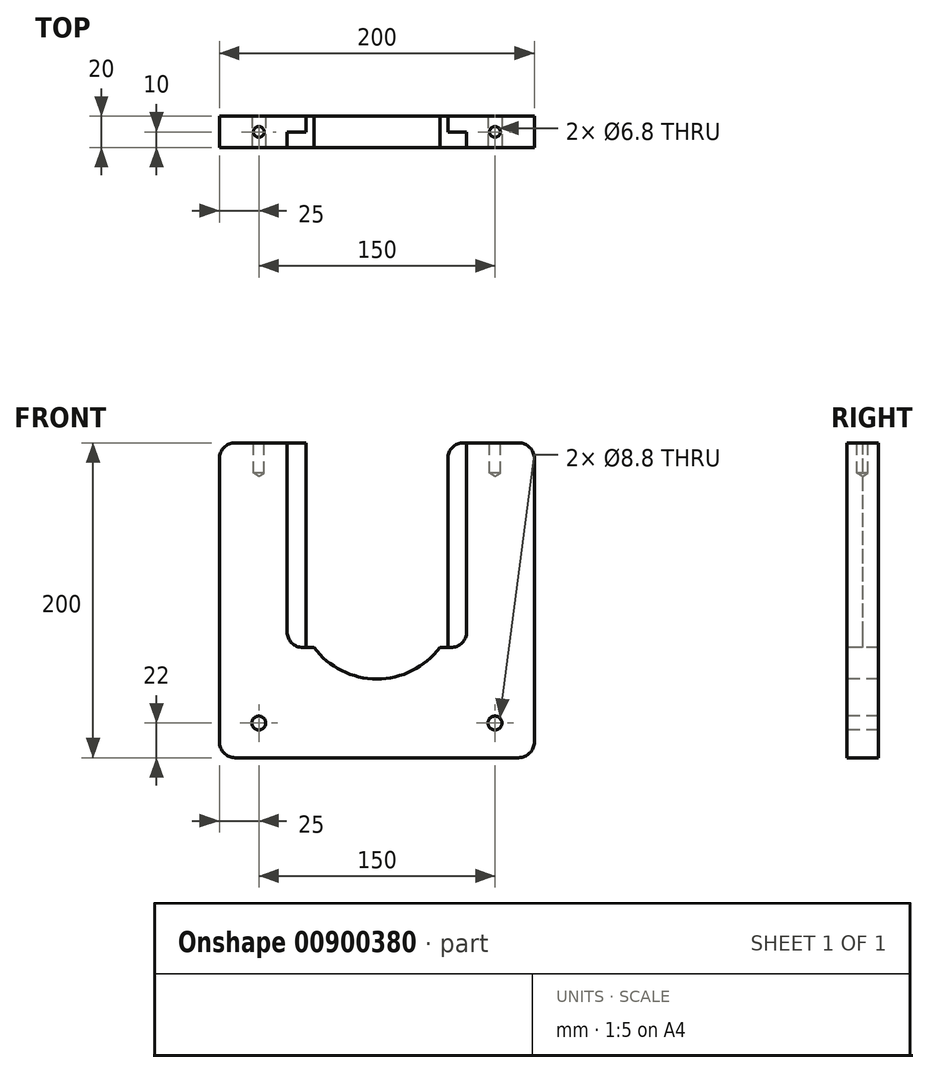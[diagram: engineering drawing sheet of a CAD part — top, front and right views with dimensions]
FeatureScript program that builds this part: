
annotation { "Feature Type Name" : "Feature", "Feature Type Description" : "" }
export const myFeature = defineFeature(function(context is Context, id is Id, definition is map)
    precondition{}
    {
        {
            var Q0;
            Q0=qCreatedBy(makeId("Front.planeOp"),FACE);
            var sketch = newSketch(context, id + "F0", { "sketchPlane" : qUnion([Q0])});
            skLineSegment(sketch, "E0.bottom", {"start": v(-100, 100) * mm, "end": v(100, 100) * mm});
            skLineSegment(sketch, "E0.top", {"start": v(-100, -100) * mm, "end": v(100, -100) * mm});
            skLineSegment(sketch, "E0.left", {"start": v(-100, 100) * mm, "end": v(-100, -100) * mm});
            skLineSegment(sketch, "E0.right", {"start": v(100, 100) * mm, "end": v(100, -100) * mm});
            skPoint(sketch, "E0.middle", {"position": v(0, 0) * mm});
            skSolve(sketch);
        }
        {
            var Q0;
            Q0=qSketchRegion(id+"F0",true);
            extrude(context, id + "F1", {"entities" : qUnion([Q0]), "endBound" : BoundingType.SYMMETRIC, "depth" : 20 * mm, "offsetDistance" : 25 * mm});
        }
        {
            var Q0;
            Q0=makeQuery(id+"F1.opExtrude","CAP_FACE",FACE,{"disambiguationData":[OSD([sQuery(id+"F0.wireOp",EDGE,"E0.bottom"),sQuery(id+"F0.wireOp",EDGE,"E0.top"),sQuery(id+"F0.wireOp",EDGE,"E0.left"),sQuery(id+"F0.wireOp",EDGE,"E0.right")])],"isStart":false});
            var sketch = newSketch(context, id + "F2", { "sketchPlane" : qUnion([Q0])});
            skCircle(sketch, "E1", {"center": v(0, 0) * mm, "radius": 15 * mm});
            skCircle(sketch, "E2", {"center": v(0, 0) * mm, "radius": 75 * mm, "construction": true});
            skSolve(sketch);
        }
        {
            var Q0;
            Q0=qSketchRegion(id+"F2",true);
            extrude(context, id + "F3", {"entities" : qUnion([Q0]), "operationType" : NewBodyOperationType.REMOVE, "endBound" : BoundingType.THROUGH_ALL, "oppositeDirection" : true, "depth" : 25 * mm, "offsetDistance" : 25 * mm});
        }
        {
            var Q0;
            Q0=makeQuery(id+"F1.opExtrude","CAP_FACE",FACE,{"disambiguationData":[OSD([sQuery(id+"F0.wireOp",EDGE,"E0.bottom"),sQuery(id+"F0.wireOp",EDGE,"E0.top"),sQuery(id+"F0.wireOp",EDGE,"E0.left"),sQuery(id+"F0.wireOp",EDGE,"E0.right")])],"isStart":false});
            var sketch = newSketch(context, id + "F4", { "sketchPlane" : qUnion([Q0])});
            skPoint(sketch, "E3", {"position": v(75, -78) * mm});
            skPoint(sketch, "E4", {"position": v(-75, -78) * mm});
            skPoint(sketch, "E5", {"position": v(0, 0) * mm});
            skSolve(sketch);
        }
        {
            var Q0;
            Q0=sQuery(id+"F4.wireOp",VERTEX,"0a962e41-9311-4d20-8398-ac3b29eb1dd7");
            var Q1;
            Q1=sQuery(id+"F4.wireOp",VERTEX,"E4");
            var Q2;
            Q2=sQuery(id+"F4.wireOp",VERTEX,"E3");
            var Q3;
            Q3=makeQuery(id+"F1.opExtrude","SWEPT_BODY",BODY,{"disambiguationData":[OSD([sQuery(id+"F0.wireOp",EDGE,"E0.bottom"),sQuery(id+"F0.wireOp",EDGE,"E0.top"),sQuery(id+"F0.wireOp",EDGE,"E0.left"),sQuery(id+"F0.wireOp",EDGE,"E0.right")])]});
            hole(context, id + "F5", {"style" : HoleStyle.SIMPLE, "endStyle" : HoleEndStyle.THROUGH, "standardTappedOrClearance" : lookupTablePath({ "standard" : "ISO", "engagement" : "75%", "pitch" : "1.25 mm", "size" : "M10", "type" : "Tapped" }), "standardBlindInLast" : lookupTablePath({ "standard" : "ISO", "engagement" : "75%", "pitch" : "1.25 mm", "size" : "M10", "type" : "Tapped" }), "holeDiameter" : 8.8 * mm, "majorDiameter" : 10 * mm, "showTappedDepth" : true, "isTappedThrough" : true, "tappedDepth" : 12 * mm, "tapClearance" : 3, "startFromSketch" : true, "locations" : qUnion([Q0, Q1, Q2]), "scope" : qUnion([Q3])});
        }
        {
            var Q0;
            Q0=makeQuery(id+"F1.opExtrude","CAP_FACE",FACE,{"disambiguationData":[OSD([sQuery(id+"F0.wireOp",EDGE,"E0.bottom"),sQuery(id+"F0.wireOp",EDGE,"E0.top"),sQuery(id+"F0.wireOp",EDGE,"E0.left"),sQuery(id+"F0.wireOp",EDGE,"E0.right")])],"isStart":false});
            var sketch = newSketch(context, id + "F6", { "sketchPlane" : qUnion([Q0])});
            skLineSegment(sketch, "E6.bottom", {"start": v(-45, 100) * mm, "end": v(45, 100) * mm});
            skLineSegment(sketch, "E6.left", {"start": v(-45, 100) * mm, "end": v(-45, -30) * mm});
            skLineSegment(sketch, "E6.right", {"start": v(45, 100) * mm, "end": v(45, -30) * mm});
            skLineSegment(sketch, "E7", {"start": v(0, 0) * mm, "end": v(0, 100) * mm, "construction": true});
            skArc(sketch, "E8", {"start": v(-40, -30) * mm, "mid": v(0, -50) * mm, "end": v(40, -30) * mm});
            skLineSegment(sketch, "E9", {"start": v(40, -30) * mm, "end": v(45, -30) * mm});
            skLineSegment(sketch, "E10", {"start": v(-40, -30) * mm, "end": v(-45, -30) * mm});
            skSolve(sketch);
        }
        {
            var Q0;
            Q0=qSketchRegion(id+"F6",true);
            extrude(context, id + "F7", {"entities" : qUnion([Q0]), "operationType" : NewBodyOperationType.REMOVE, "endBound" : BoundingType.THROUGH_ALL, "oppositeDirection" : true, "depth" : 25 * mm, "offsetDistance" : 25 * mm});
        }
        {
            var Q0;
            Q0=makeQuery(id+"F1.opExtrude","CAP_FACE",FACE,{"disambiguationData":[OSD([sQuery(id+"F0.wireOp",EDGE,"E0.bottom"),sQuery(id+"F0.wireOp",EDGE,"E0.top"),sQuery(id+"F0.wireOp",EDGE,"E0.left"),sQuery(id+"F0.wireOp",EDGE,"E0.right")])],"isStart":false});
            var sketch = newSketch(context, id + "F8", { "sketchPlane" : qUnion([Q0])});
            skLineSegment(sketch, "E11.bottom", {"start": v(-57, 100) * mm, "end": v(-45, 100) * mm});
            skLineSegment(sketch, "E11.top", {"start": v(-57, -30) * mm, "end": v(-45, -30) * mm});
            skLineSegment(sketch, "E11.left", {"start": v(-57, 100) * mm, "end": v(-57, -30) * mm});
            skLineSegment(sketch, "E11.right", {"start": v(-45, 100) * mm, "end": v(-45, -30) * mm});
            skLineSegment(sketch, "E12.bottom", {"start": v(57, 100) * mm, "end": v(45, 100) * mm});
            skLineSegment(sketch, "E12.top", {"start": v(57, -30) * mm, "end": v(45, -30) * mm});
            skLineSegment(sketch, "E12.left", {"start": v(57, 100) * mm, "end": v(57, -30) * mm});
            skLineSegment(sketch, "E12.right", {"start": v(45, 100) * mm, "end": v(45, -30) * mm});
            skSolve(sketch);
        }
        {
            var Q0;
            Q0=qSketchRegion(id+"F8",true);
            extrude(context, id + "F9", {"entities" : qUnion([Q0]), "operationType" : NewBodyOperationType.REMOVE, "oppositeDirection" : true, "depth" : 10 * mm, "offsetDistance" : 25 * mm});
        }
        {
            var Q0;
            Q0=makeQuery(id+"F1.opExtrude","SWEPT_EDGE",EDGE,{"disambiguationData":[OSD([sQuery(id+"F0.wireOp",EDGE,"E0.bottom"),sQuery(id+"F0.wireOp",EDGE,"E0.left")])]});
            var Q1;
            Q1=makeQuery(id+"F7.boolean.opBoolean","COPY",EDGE,{"derivedFrom":makeQuery(id+"F7.opExtrude","SWEPT_EDGE",EDGE,{"disambiguationData":[OSD([sQuery(id+"F0.wireOp",EDGE,"E0.bottom"),sQuery(id+"F6.wireOp",EDGE,"E6.bottom"),sQuery(id+"F6.wireOp",EDGE,"E6.left")])]})});
            var Q2;
            Q2=makeQuery(id+"F7.boolean.opBoolean","COPY",EDGE,{"derivedFrom":makeQuery(id+"F7.opExtrude","SWEPT_EDGE",EDGE,{"disambiguationData":[OSD([sQuery(id+"F0.wireOp",EDGE,"E0.bottom"),sQuery(id+"F6.wireOp",EDGE,"E6.bottom"),sQuery(id+"F6.wireOp",EDGE,"E6.right")])]})});
            var Q3;
            Q3=makeQuery(id+"F1.opExtrude","SWEPT_EDGE",EDGE,{"disambiguationData":[OSD([sQuery(id+"F0.wireOp",EDGE,"E0.bottom"),sQuery(id+"F0.wireOp",EDGE,"E0.right")])]});
            var Q4;
            Q4=makeQuery(id+"F1.opExtrude","SWEPT_EDGE",EDGE,{"disambiguationData":[OSD([sQuery(id+"F0.wireOp",EDGE,"E0.top"),sQuery(id+"F0.wireOp",EDGE,"E0.right")])]});
            var Q5;
            Q5=makeQuery(id+"F1.opExtrude","SWEPT_EDGE",EDGE,{"disambiguationData":[OSD([sQuery(id+"F0.wireOp",EDGE,"E0.top"),sQuery(id+"F0.wireOp",EDGE,"E0.left")])]});
            var Q6;
            Q6=makeQuery(id+"FdCRteI6IR7YTnl_1.boolean.opBoolean","COPY",EDGE,{"derivedFrom":makeQuery(id+"FdCRteI6IR7YTnl_1.opExtrude","SWEPT_EDGE",EDGE,{"disambiguationData":[OSD([sQuery(id+"F0.wireOp",EDGE,"E0.bottom"),sQuery(id+"FyoQDDeGrXr7jXy_1.wireOp",EDGE,"F9jeVxsr-ByuF-WkVe-5R6b-Y215I5nIABxF.bottom"),sQuery(id+"FyoQDDeGrXr7jXy_1.wireOp",EDGE,"F9jeVxsr-ByuF-WkVe-5R6b-Y215I5nIABxF.right")])]})});
            var Q7;
            Q7=makeQuery(id+"FdCRteI6IR7YTnl_1.boolean.opBoolean","COPY",EDGE,{"derivedFrom":makeQuery(id+"FdCRteI6IR7YTnl_1.opExtrude","SWEPT_EDGE",EDGE,{"disambiguationData":[OSD([sQuery(id+"F0.wireOp",EDGE,"E0.top"),sQuery(id+"FyoQDDeGrXr7jXy_1.wireOp",EDGE,"F9jeVxsr-ByuF-WkVe-5R6b-Y215I5nIABxF.top"),sQuery(id+"FyoQDDeGrXr7jXy_1.wireOp",EDGE,"F9jeVxsr-ByuF-WkVe-5R6b-Y215I5nIABxF.right")])]})});
            fillet(context, id + "F10", {"entities" : qUnion([Q0, Q1, Q2, Q3, Q4, Q5, Q6, Q7]), "radius" : 10 * mm, "tangentPropagation" : true, "allowEdgeOverflow" : false});
        }
        {
            var Q0;
            Q0=makeQuery(id+"F9.boolean.opBoolean","COPY",EDGE,{"derivedFrom":makeQuery(id+"F9.opExtrude","SWEPT_EDGE",EDGE,{"disambiguationData":[OSD([sQuery(id+"F8.wireOp",EDGE,"E11.top"),sQuery(id+"F8.wireOp",EDGE,"E11.left")])]})});
            var Q1;
            Q1=makeQuery(id+"F9.boolean.opBoolean","COPY",EDGE,{"derivedFrom":makeQuery(id+"F9.opExtrude","SWEPT_EDGE",EDGE,{"disambiguationData":[OSD([sQuery(id+"F8.wireOp",EDGE,"E12.top"),sQuery(id+"F8.wireOp",EDGE,"E12.left")])]})});
            fillet(context, id + "F11", {"entities" : qUnion([Q0, Q1]), "radius" : 10 * mm, "tangentPropagation" : true, "allowEdgeOverflow" : false});
        }
        {
            var Q0;
            {var subQ1=sQuery(id+"F0.wireOp",EDGE,"E0.left");var subQ3=sQuery(id+"F0.wireOp",EDGE,"E0.bottom");Q0=makeQuery(id+"F7.boolean.opBoolean","SPLIT",FACE,{"disambiguationData":[TD([makeQuery(id+"F1.opExtrude","SWEPT_FACE",FACE,{"disambiguationData":[OSD([subQ1])]})])],"derivedFrom":makeQuery(id+"F1.opExtrude","SWEPT_FACE",FACE,{"disambiguationData":[OSD([subQ3])]})});}
            var sketch = newSketch(context, id + "F12", { "sketchPlane" : qUnion([Q0])});
            skPoint(sketch, "E13", {"position": v(-75, 0) * mm});
            skPoint(sketch, "E14", {"position": v(75, 0) * mm});
            skSolve(sketch);
        }
        {
            var Q0;
            Q0=sQuery(id+"F12.wireOp",VERTEX,"E13");
            var Q1;
            Q1=sQuery(id+"F12.wireOp",VERTEX,"E14");
            var Q2;
            Q2=makeQuery(id+"F1.opExtrude","SWEPT_BODY",BODY,{"disambiguationData":[OSD([sQuery(id+"F0.wireOp",EDGE,"E0.bottom"),sQuery(id+"F0.wireOp",EDGE,"E0.top"),sQuery(id+"F0.wireOp",EDGE,"E0.left"),sQuery(id+"F0.wireOp",EDGE,"E0.right")])]});
            hole(context, id + "F13", {"style" : HoleStyle.SIMPLE, "endStyle" : HoleEndStyle.BLIND, "standardTappedOrClearance" : lookupTablePath({ "standard" : "ISO", "engagement" : "75%", "pitch" : "1.25 mm", "size" : "M8", "type" : "Tapped" }), "standardBlindInLast" : lookupTablePath({ "standard" : "ISO", "engagement" : "75%", "pitch" : "1.25 mm", "size" : "M8", "type" : "Tapped" }), "holeDiameter" : 6.8 * mm, "majorDiameter" : 8 * mm, "showTappedDepth" : true, "holeDepth" : 19.25 * mm, "isTappedThrough" : true, "tappedDepth" : 15.5 * mm, "tapClearance" : 3, "startFromSketch" : true, "locations" : qUnion([Q0, Q1]), "scope" : qUnion([Q2])});
        }
    });
